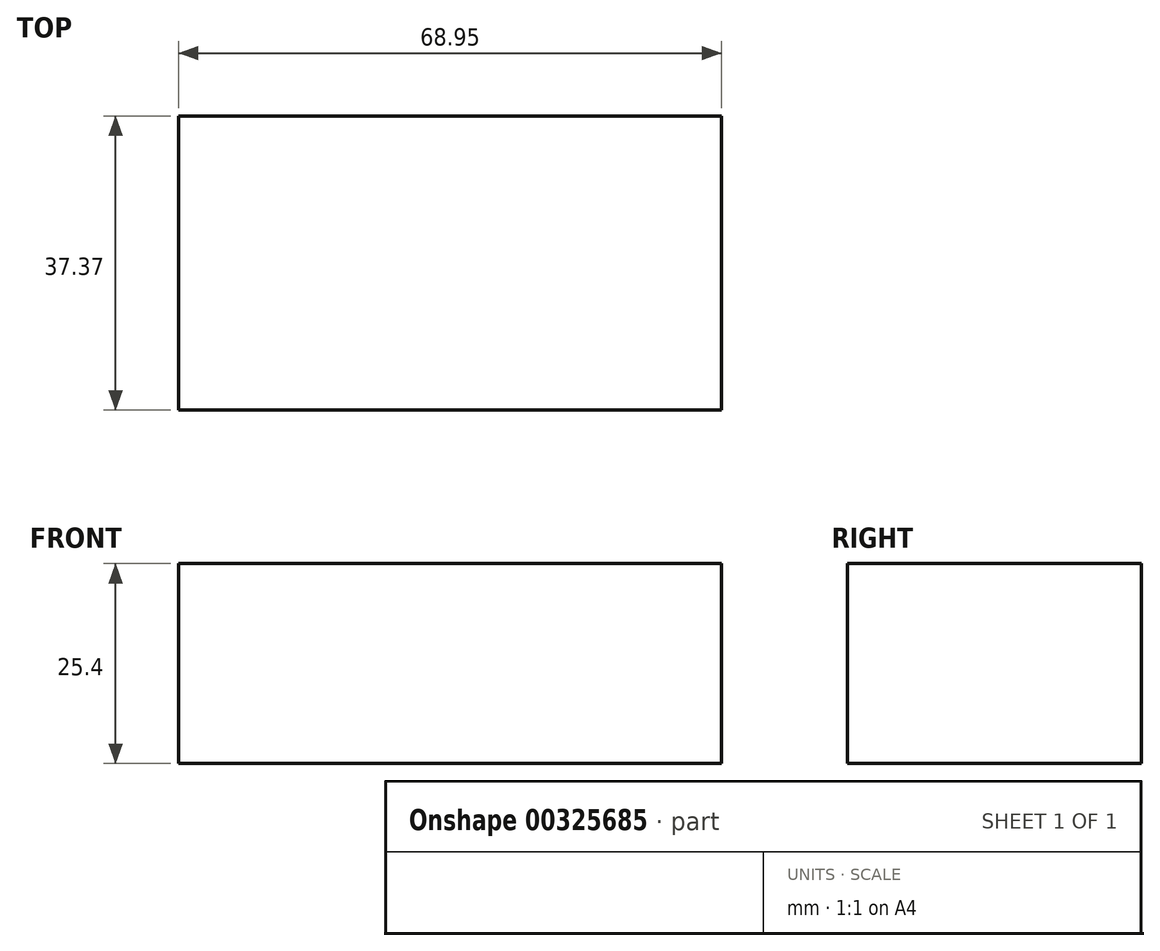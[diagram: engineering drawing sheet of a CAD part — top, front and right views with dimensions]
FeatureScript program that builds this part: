
annotation { "Feature Type Name" : "Feature", "Feature Type Description" : "" }
export const myFeature = defineFeature(function(context is Context, id is Id, definition is map)
    precondition{}
    {
        {
            var Q0;
            Q0=qCreatedBy(makeId("Top.planeOp"),FACE);
            var sketch = newSketch(context, id + "F0", { "sketchPlane" : qUnion([Q0])});
            skLineSegment(sketch, "E0.bottom", {"start": v(-25, 14.74) * mm, "end": v(43.95, 14.74) * mm});
            skLineSegment(sketch, "E0.top", {"start": v(-25, -22.63) * mm, "end": v(43.95, -22.63) * mm});
            skLineSegment(sketch, "E0.left", {"start": v(-25, 14.74) * mm, "end": v(-25, -22.63) * mm});
            skLineSegment(sketch, "E0.right", {"start": v(43.95, 14.74) * mm, "end": v(43.95, -22.63) * mm});
            skSolve(sketch);
        }
        {
            var Q0;
            Q0=makeQuery(id+"F0.imprint","IMPRINT",FACE,{"disambiguationData":[TD([[makeQuery(id+"F0.imprint","IMPRINT",EDGE,{"derivedFrom":sQuery(id+"F0.wireOp",EDGE,"E0.bottom")}),-1.0]])]});
            extrude(context, id + "F1", {"entities" : qUnion([Q0]), "depth" : 25.4 * mm});
        }
    });
